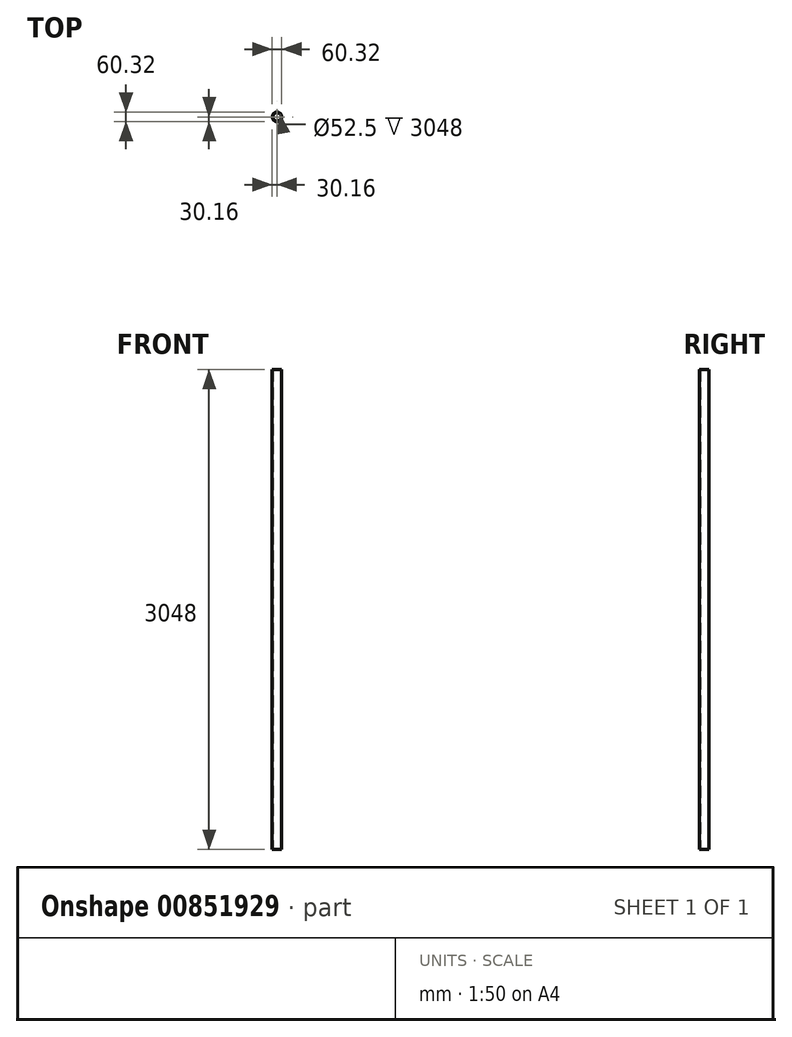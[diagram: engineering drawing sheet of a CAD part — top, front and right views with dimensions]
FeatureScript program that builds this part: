
annotation { "Feature Type Name" : "Feature", "Feature Type Description" : "" }
export const myFeature = defineFeature(function(context is Context, id is Id, definition is map)
    precondition{}
    {
        {
            var Q0;
            Q0=qCreatedBy(makeId("Top.planeOp"),FACE);
            var sketch = newSketch(context, id + "F0", { "sketchPlane" : qUnion([Q0])});
            skCircle(sketch, "E0", {"center": v(0, 0) * mm, "radius": 30.16 * mm});
            skCircle(sketch, "E1", {"center": v(0, 0) * mm, "radius": 26.25 * mm});
            skSolve(sketch);
        }
        {
            var Q0;
            Q0 = qSketchRegion(id + "F0", true);
            extrude(context, id + "F1", {"entities" : qUnion([Q0]), "depth" : 3048 * mm, "offsetDistance" : 25.4 * mm});
        }
    });
